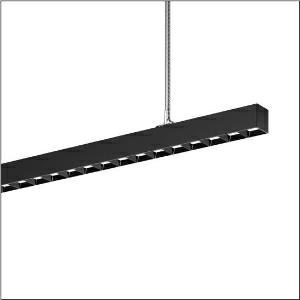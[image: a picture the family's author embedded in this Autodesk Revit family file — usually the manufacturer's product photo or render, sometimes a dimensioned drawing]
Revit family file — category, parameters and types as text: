
# Revit family: silica_r__21_51mx34dc3dbb_b9b0
name_source: partatom
category: Lighting Fixtures
units: mm (PartAtom-declared; Revit-internal decimal feet)

## family parameters
Cut with Voids When Loaded = No
Host = Face
Light Source = No
Part Type = Normal
Room Calculation Point = No
Round Connector Dimension = Use Diameter
Shared = No

## types (1)
- --- (1 x LED, 19200 lm, 129.1 W, 3000K)
    Apparent Load = 129 VA
    CIE Flux Codes = 74 94 99 56 100
    Color Rendering = 80
    Color Temperature = 3000K
    Default Elevation = 1800 mm
    Description = Silica® 21, office luminaire, primary light control with darklight reflector, of PMMA, black, light emission: direct/indirect distribution, primary light characteristic: asymmetric, installation type: suspended mounting, LED, rated luminous flux: 19.200lm, luminous efficacy: 149lm/W, light colour: 830, colour temperature: 3000K, with terminal, 3+2-pole, max. 2.5mm², mains connection: 220..240V, AC, 50/60Hz, rated input power: 129.1W, luminaire housing, of aluminium, jet black (RAL 9005), length: 3.004mm, width: 53mm, height: 53mm, protection rating (complete): IP20, insulation class (complete): insulation class I (protective earthing), certification: CE, permissible operating ambient temperature: 0..+35°C, standard: EN 50419, packaging unit: 1 piece
    Height = 53 mm
    Lamp = 1 x LED
    Lamp Light Flux = 19200 lm
    Lamp Power = 129.1 W
    Lamp count = 1
    Length = 3004 mm
    Luminous efficacy = 149 lm/W
    Manufacturer = Siteco
    ModVariant = No
    Model = 51MX34DC3DBB
    Mounting Place = Ceiling
    Mounting Type = Pendant
    Number of Poles = 1
    OnlyDefault = Yes
    Power Factor = 1
    Product Name = Silica® 21
    Product group = office luminaire | ceiling pendant
    ProductGroupID = 902
    Protection Class = Protection class I
    Protection Degree = IP 20
    RLX_Detail_Level = 1
    RLX_Emergency_Light_Flux = 0 lm
    RLX_Emergency_Type = 0
    RLX_Emergency_Type_DB = No
    RlxData = <blob elided: 67805 chars, md5=d315d7b2>
    Socket = socket
    Standby Power = 0 W
    System Light Flux = 19200 lm
    System Power = 129 W
    Type Comments = factory setting: luminous flux: 100 % | dim-lin: 254 | 448 mA
    Type Image = l_1297774.jpg
    URL = http://relux.com
    VarID = @adj_050747
    Voltage = 0 V
    Weight = 0.00 kg
    Width = 53 mm

## geometry (parser evidence)
native form markers: Blend x4, Sweep x12
no freeform markers — native parametric forms only
